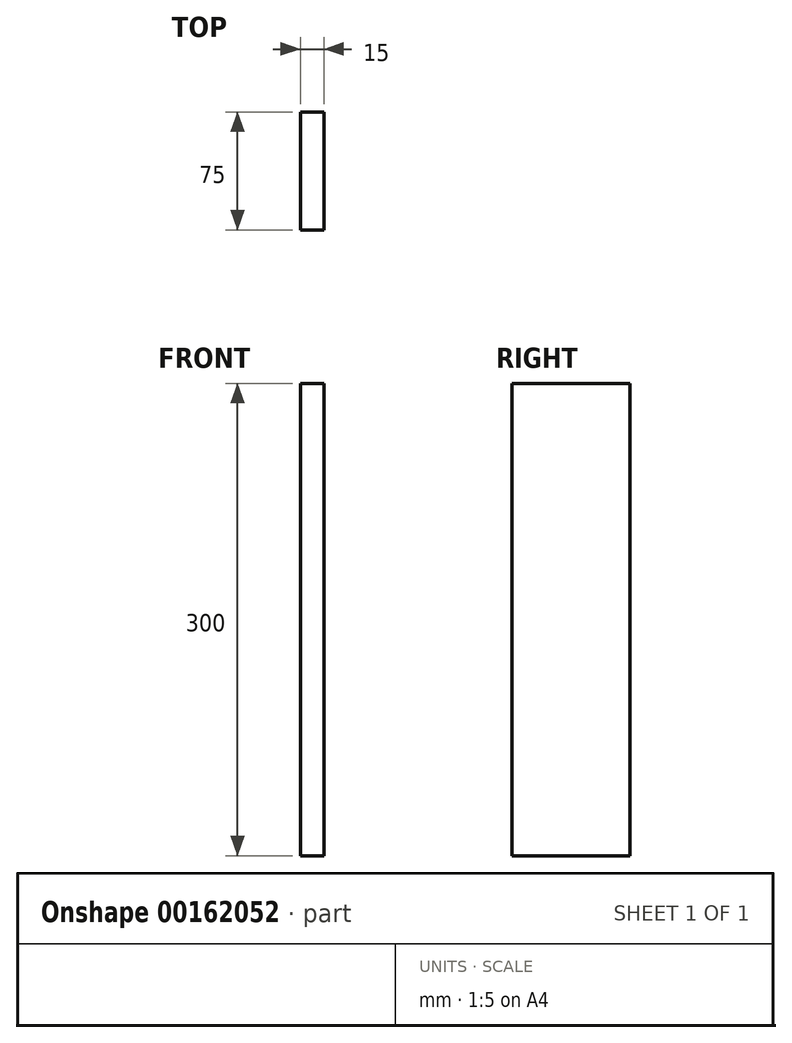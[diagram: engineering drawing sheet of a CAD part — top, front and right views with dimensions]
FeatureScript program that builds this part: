
annotation { "Feature Type Name" : "Feature", "Feature Type Description" : "" }
export const myFeature = defineFeature(function(context is Context, id is Id, definition is map)
    precondition{}
    {
        {
            var Q0;
            Q0=qCreatedBy(makeId("Right.planeOp"),FACE);
            var sketch = newSketch(context, id + "F0", { "sketchPlane" : qUnion([Q0])});
            skLineSegment(sketch, "E0", {"start": v(0, 300) * mm, "end": v(0, 0) * mm});
            skLineSegment(sketch, "E1", {"start": v(0, 0) * mm, "end": v(-75, 0) * mm});
            skLineSegment(sketch, "E2", {"start": v(-75, 0) * mm, "end": v(-75, 300) * mm});
            skLineSegment(sketch, "E3", {"start": v(0, 300) * mm, "end": v(-75, 300) * mm});
            skSolve(sketch);
        }
        {
            var Q0;
            Q0=makeQuery(id+"F0.imprint","IMPRINT",FACE,{"disambiguationData":[TD([[makeQuery(id+"F0.imprint","IMPRINT",EDGE,{"derivedFrom":sQuery(id+"F0.wireOp",EDGE,"E0")}),-1.0]])]});
            extrude(context, id + "F1", {"entities" : qUnion([Q0]), "depth" : 15 * mm});
        }
    });
